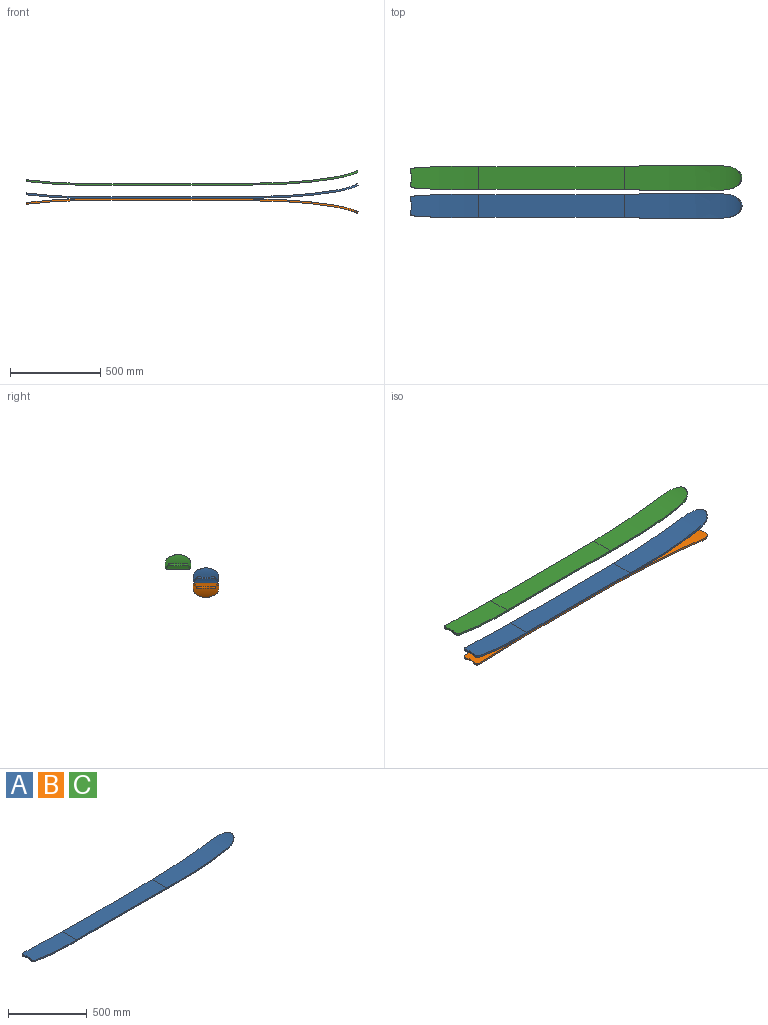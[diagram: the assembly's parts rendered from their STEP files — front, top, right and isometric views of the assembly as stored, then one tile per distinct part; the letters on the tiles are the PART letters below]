
ASSEMBLY  parts=3 mates=1
PART A: 22 faces, bbox 1838.5x141x81.7 mm
  f0: bspline ~62.58x10.83mm, area 643.2mm2, adj f1,f15,f16,f19
  f1: bspline ~23.57x16.75mm, area 319.7mm2, adj f0,f2,f16,f19
  f2: bspline ~285.9x28.78mm, area 2862.1mm2, adj f1,f3,f16,f19
  f3: bspline ~79.81x10.77mm, area 797.3mm2, adj f2,f4,f16,f19
  f4: cylinder r=31912.86mm len=807.57mm, axis (0,0,1), area 8075.9mm2, adj f3,f5,f17,f20
  f5: bspline ~247.16x16.78mm, area 2470.3mm2, adj f4,f6,f18,f21
  f6: bspline ~282.59x40.28mm, area 2832.4mm2, adj f5,f7,f18,f21
  f7: bspline ~37.02x16.93mm, area 358.1mm2, adj f6,f8,f18,f21
  f8: bspline ~131.06x87.82mm, area 2401.4mm2, adj f7,f9,f18,f21
  f9: bspline ~37.02x16.93mm, area 358.1mm2, adj f8,f10,f18,f21
  f10: bspline ~282.59x40.28mm, area 2832.4mm2, adj f9,f11,f18,f21
  f11: bspline ~247.16x16.78mm, area 2470.3mm2, adj f10,f12,f18,f21
  f12: cylinder r=31912.86mm len=807.57mm, axis (0,0,1), area 8075.9mm2, adj f11,f13,f17,f20
  f13: bspline ~79.81x10.77mm, area 797.3mm2, adj f12,f14,f16,f19
  f14: bspline ~285.9x28.78mm, area 2862.1mm2, adj f13,f15,f16,f19
  f15: bspline ~23.57x16.79mm, area 319.7mm2, adj f0,f14,f16,f19
  f16: extruded ~379.39x131mm, area 47212mm2, adj f0,f1,f2,f3,f13,f14,f15,f17
  f17: plane 807.57x129.94mm, normal (0,0,1), area 101539.9mm2, adj f4,f12,f16,f18
  f18: extruded ~645.01x141mm, area 85986.4mm2, adj f5,f6,f7,f8,f9,f10,f11,f17
  f19: extruded ~380.89x131mm, area 47391.8mm2, adj f0,f1,f2,f3,f13,f14,f15,f20
  f20: plane 807.57x129.94mm, normal (0,0,-1), area 101539.9mm2, adj f4,f12,f19,f21
  f21: extruded ~650.01x141mm, area 86521.1mm2, adj f5,f6,f7,f8,f9,f10,f11,f20
PART B: same geometry as A
PART C: same geometry as A
PLACE A t=(-195.65,-385.39,164.84)mm
PLACE B rot(axis=(1,0,0),180deg) t=(-195.65,-385.39,-15.16)mm
PLACE C t=(-195.68,-230.48,238.45)mm
MATE fastened B.f20 <-> A.f20  axis (0,0,1) through (-958.58,-385.39,74.84)mm
